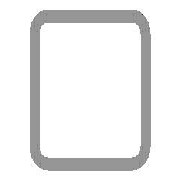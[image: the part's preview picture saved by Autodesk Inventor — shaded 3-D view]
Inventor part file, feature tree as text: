
AUTODESK INVENTOR PART (.ipt)
format: ipt  version: 2025 (Build 290162010, 162A)  size: 133,120 bytes
history: native  units: mm (DEFAULTED — no unit token found)
features: other x4, sketch x1, plane x1
ambient origin geometry x8: Origin, YZ Plane, XZ Plane, XY Plane, X Axis, Y Axis, Z Axis, Center Point
bodies: Solid1 (feature_tree), Body (feature_tree)
feature tree (6):
  parser-record x1  (decoder bookkeeping rows leaked as tree rows — omitted from the tree; the rows remain in map.json)
  other  "Driven Length"
  other  "Start Plane"
  other  "End Plane"
  sketch  "Sketch3"  dims[d3=2920.0mm d4=0.0mm d7=4.0mm d9=40.0mm d11=40.0mm d12=2.0mm d13=-0.0mm d14=2920.0mm d15=20.0mm d16=20.0mm d17=90.0deg d18=2920.0mm]
  plane  "Work Plane3"
